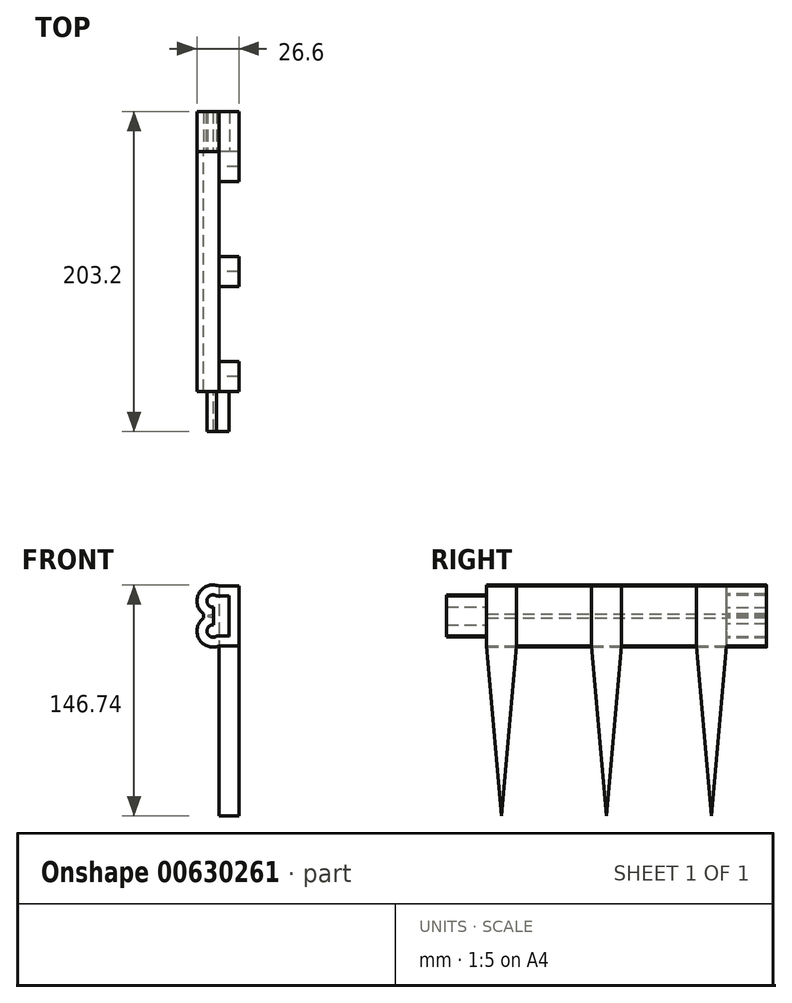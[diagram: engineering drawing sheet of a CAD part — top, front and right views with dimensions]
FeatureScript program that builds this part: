
annotation { "Feature Type Name" : "Feature", "Feature Type Description" : "" }
export const myFeature = defineFeature(function(context is Context, id is Id, definition is map)
    precondition{}
    {
        {
            var Q0;
            Q0=qCreatedBy(makeId("Front.planeOp"),FACE);
            var sketch = newSketch(context, id + "F0", { "sketchPlane" : qUnion([Q0])});
            skLineSegment(sketch, "E0", {"start": v(-11.64, 12.37) * mm, "end": v(-11.64, -25.73) * mm});
            skArc(sketch, "E1", {"start": v(-11.64, 12.37) * mm, "mid": v(-25.54, 2.85) * mm, "end": v(-11.64, -6.68) * mm});
            skArc(sketch, "E2", {"start": v(-11.64, -6.68) * mm, "mid": v(-25.54, -16.2) * mm, "end": v(-11.64, -25.73) * mm});
            skLineSegment(sketch, "E3", {"start": v(-21.3, -5.44) * mm, "end": v(-21.3, -7.92) * mm});
            skSolve(sketch);
        }
        {
            var Q0;
            Q0 = qSketchRegion(id + "F0", true);
            extrude(context, id + "F1", {"entities" : qUnion([Q0]), "depth" : 152.4 * mm, "offsetDistance" : 25.4 * mm});
        }
        {
            var Q0;
            Q0=makeQuery(id+"F1.opExtrude","SWEPT_FACE",FACE,{"disambiguationData":[OSD([sQuery(id+"F0.wireOp",EDGE,"E0")])]});
            var sketch = newSketch(context, id + "F2", { "sketchPlane" : qUnion([Q0])});
            skLineSegment(sketch, "E4", {"start": v(-133.35, 12.37) * mm, "end": v(-133.35, -25.73) * mm});
            skLineSegment(sketch, "E5", {"start": v(-85.73, 12.37) * mm, "end": v(-85.73, -25.73) * mm});
            skLineSegment(sketch, "E6", {"start": v(-66.68, 12.37) * mm, "end": v(-66.68, -25.73) * mm});
            skLineSegment(sketch, "E7", {"start": v(-19.05, 12.37) * mm, "end": v(-19.05, -25.73) * mm});
            skLineSegment(sketch, "E8", {"start": v(-152.4, -25.73) * mm, "end": v(-142.88, -133.68) * mm});
            skLineSegment(sketch, "E9", {"start": v(-142.88, -133.68) * mm, "end": v(-133.35, -25.73) * mm});
            skLineSegment(sketch, "E10", {"start": v(-85.73, -25.73) * mm, "end": v(-76.2, -133.68) * mm});
            skLineSegment(sketch, "E11", {"start": v(-76.2, -133.68) * mm, "end": v(-66.67, -25.73) * mm});
            skLineSegment(sketch, "E12", {"start": v(0, -25.73) * mm, "end": v(-9.52, -133.68) * mm});
            skLineSegment(sketch, "E13", {"start": v(-9.52, -133.68) * mm, "end": v(-19.05, -25.73) * mm});
            skSolve(sketch);
        }
        {
            var Q0;
            {var subQ0=sQuery(id+"F2.wireOp",EDGE,"E12");Q0=makeQuery(id+"F2.imprint","IMPRINT",FACE,{"disambiguationData":[TD([[makeQuery(id+"F2.imprint","IMPRINT",EDGE,{"derivedFrom":subQ0}),-1.0]])]});}
            var Q1;
            {var subQ0=sQuery(id+"F2.wireOp",EDGE,"E7");Q1=makeQuery(id+"F2.imprint","IMPRINT",FACE,{"disambiguationData":[TD([[makeQuery(id+"F2.imprint","IMPRINT",EDGE,{"derivedFrom":subQ0}),1.0]])]});}
            var Q2;
            {var subQ0=sQuery(id+"F2.wireOp",EDGE,"E10");Q2=makeQuery(id+"F2.imprint","IMPRINT",FACE,{"disambiguationData":[TD([[makeQuery(id+"F2.imprint","IMPRINT",EDGE,{"derivedFrom":subQ0}),1.0]])]});}
            var Q3;
            {var subQ0=sQuery(id+"F2.wireOp",EDGE,"E5");Q3=makeQuery(id+"F2.imprint","IMPRINT",FACE,{"disambiguationData":[TD([[makeQuery(id+"F2.imprint","IMPRINT",EDGE,{"derivedFrom":subQ0}),1.0]])]});}
            var Q4;
            {var subQ0=sQuery(id+"F2.wireOp",EDGE,"E4");Q4=makeQuery(id+"F2.imprint","IMPRINT",FACE,{"disambiguationData":[TD([[makeQuery(id+"F2.imprint","IMPRINT",EDGE,{"derivedFrom":subQ0}),-1.0]])]});}
            var Q5;
            {var subQ0=sQuery(id+"F2.wireOp",EDGE,"E8");Q5=makeQuery(id+"F2.imprint","IMPRINT",FACE,{"disambiguationData":[TD([[makeQuery(id+"F2.imprint","IMPRINT",EDGE,{"derivedFrom":subQ0}),1.0]])]});}
            extrude(context, id + "F3", {"entities" : qUnion([Q0, Q1, Q2, Q3, Q4, Q5]), "operationType" : NewBodyOperationType.ADD, "depth" : 12.7 * mm, "offsetDistance" : 25.4 * mm});
        }
        {
            var Q0;
            {var subQ0=sQuery(id+"F0.wireOp",EDGE,"E0");Q0=makeQuery(id+"F3.boolean.opBoolean","MERGE",FACE,{"derivedFrom":[makeQuery(id+"F1.opExtrude","CAP_FACE",FACE,{"disambiguationData":[OSD([subQ0,sQuery(id+"F0.wireOp",EDGE,"E1"),sQuery(id+"F0.wireOp",EDGE,"E2"),sQuery(id+"F0.wireOp",EDGE,"E3")])],"isStart":false}),makeQuery(id+"F3.opExtrude","SWEPT_FACE",FACE,{"disambiguationData":[OSD([subQ0]),TDD([makeQuery(id+"F2.imprint","IMPRINT",EDGE,{"derivedFrom":makeQuery(id+"F1.opExtrude","CAP_EDGE",EDGE,{"disambiguationData":[OSD([subQ0])],"isStart":false})})])]})]});}
            var sketch = newSketch(context, id + "F4", { "sketchPlane" : qUnion([Q0])});
            skLineSegment(sketch, "E14.0", {"start": v(-5.3, 6.02) * mm, "end": v(-13.13, 6.02) * mm});
            skLineSegment(sketch, "E14.1", {"start": v(-14.95, -1) * mm, "end": v(-14.95, -12.36) * mm});
            skArc(sketch, "E14.2", {"start": v(-14.95, -12.36) * mm, "mid": v(-19.07, -17.17) * mm, "end": v(-13.13, -19.38) * mm});
            skArc(sketch, "E14.3", {"start": v(-13.13, 6.02) * mm, "mid": v(-19.07, 3.82) * mm, "end": v(-14.95, -1) * mm});
            skLineSegment(sketch, "E14.4", {"start": v(-13.13, -19.38) * mm, "end": v(-5.3, -19.38) * mm});
            skLineSegment(sketch, "E14.5", {"start": v(-5.3, -19.38) * mm, "end": v(-5.3, 6.02) * mm});
            skSolve(sketch);
        }
        {
            var Q0;
            Q0=makeQuery(id+"F4.imprint","IMPRINT",FACE,{"disambiguationData":[TD([[makeQuery(id+"F4.imprint","IMPRINT",EDGE,{"derivedFrom":sQuery(id+"F4.wireOp",EDGE,"E14.0")}),1.0]])]});
            extrude(context, id + "F5", {"entities" : qUnion([Q0]), "operationType" : NewBodyOperationType.ADD, "depth" : 25.4 * mm, "offsetDistance" : 25.4 * mm});
        }
        {
            var Q0;
            {var subQ0=sQuery(id+"F0.wireOp",EDGE,"E0");Q0=makeQuery(id+"F3.boolean.opBoolean","MERGE",FACE,{"derivedFrom":[makeQuery(id+"F1.opExtrude","CAP_FACE",FACE,{"disambiguationData":[OSD([subQ0,sQuery(id+"F0.wireOp",EDGE,"E1"),sQuery(id+"F0.wireOp",EDGE,"E2"),sQuery(id+"F0.wireOp",EDGE,"E3")])],"isStart":true}),makeQuery(id+"F3.opExtrude","SWEPT_FACE",FACE,{"disambiguationData":[OSD([subQ0]),TDD([makeQuery(id+"F2.imprint","IMPRINT",EDGE,{"derivedFrom":makeQuery(id+"F1.opExtrude","CAP_EDGE",EDGE,{"disambiguationData":[OSD([subQ0])],"isStart":true})})])]})]});}
            var sketch = newSketch(context, id + "F6", { "sketchPlane" : qUnion([Q0])});
            skLineSegment(sketch, "E15", {"start": v(-1.06, 12.37) * mm, "end": v(-1.06, -25.73) * mm});
            skLineSegment(sketch, "E16", {"start": v(-1.06, -25.73) * mm, "end": v(11.64, -25.73) * mm});
            skLineSegment(sketch, "E17", {"start": v(11.64, 12.37) * mm, "end": v(-1.06, 12.37) * mm});
            skArc(sketch, "E18", {"start": v(11.64, -6.68) * mm, "mid": v(25.5, 2.85) * mm, "end": v(11.64, 12.37) * mm});
            skArc(sketch, "E19", {"start": v(11.64, -25.73) * mm, "mid": v(25.5, -16.2) * mm, "end": v(11.64, -6.68) * mm});
            skLineSegment(sketch, "E20", {"start": v(21.3, -4.53) * mm, "end": v(21.3, -8.68) * mm});
            skLineSegment(sketch, "E21.0", {"start": v(15.46, -11.83) * mm, "end": v(15.46, -1.52) * mm});
            skLineSegment(sketch, "E21.1", {"start": v(12.97, 6.53) * mm, "end": v(4.78, 6.53) * mm});
            skLineSegment(sketch, "E21.2", {"start": v(4.78, 6.53) * mm, "end": v(4.78, -19.88) * mm});
            skArc(sketch, "E21.3", {"start": v(15.46, -1.52) * mm, "mid": v(19.5, 4.14) * mm, "end": v(12.97, 6.53) * mm});
            skLineSegment(sketch, "E21.4", {"start": v(4.78, -19.88) * mm, "end": v(12.97, -19.88) * mm});
            skArc(sketch, "E21.5", {"start": v(12.97, -19.88) * mm, "mid": v(19.5, -17.5) * mm, "end": v(15.46, -11.83) * mm});
            skSolve(sketch);
        }
        {
            var Q0;
            Q0 = qSketchRegion(id + "F6", true);
            extrude(context, id + "F7", {"entities" : qUnion([Q0]), "operationType" : NewBodyOperationType.ADD, "depth" : 25.4 * mm, "offsetDistance" : 25.4 * mm});
        }
    });
